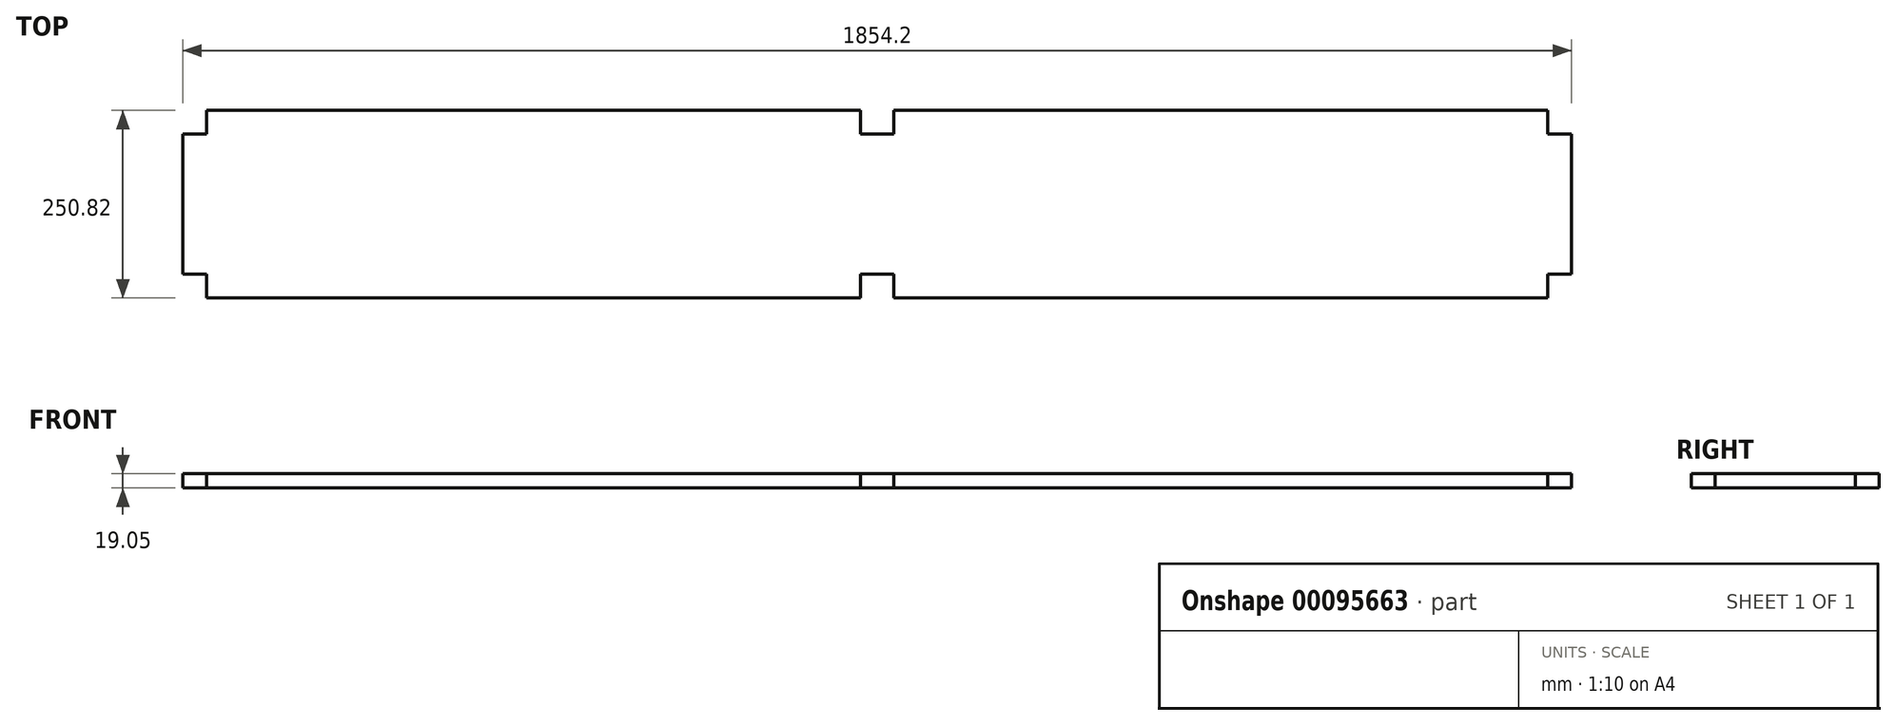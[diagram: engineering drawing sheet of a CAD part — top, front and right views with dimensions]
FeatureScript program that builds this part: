
annotation { "Feature Type Name" : "Feature", "Feature Type Description" : "" }
export const myFeature = defineFeature(function(context is Context, id is Id, definition is map)
    precondition{}
    {
        {
            var Q0;
            Q0=qCreatedBy(makeId("Top.planeOp"),FACE);
            var sketch = newSketch(context, id + "F0", { "sketchPlane" : qUnion([Q0])});
            skLineSegment(sketch, "E0.top", {"start": v(-895.35, 125.41) * mm, "end": v(-22.22, 125.41) * mm});
            skLineSegment(sketch, "E0.left", {"start": v(-927.1, -93.66) * mm, "end": v(-927.1, 93.66) * mm});
            skLineSegment(sketch, "E0.right", {"start": v(927.1, -93.66) * mm, "end": v(927.1, 93.66) * mm});
            skLineSegment(sketch, "E1", {"start": v(895.35, -125.41) * mm, "end": v(22.23, -125.41) * mm});
            skLineSegment(sketch, "E2.top", {"start": v(-927.1, 93.66) * mm, "end": v(-895.35, 93.66) * mm});
            skLineSegment(sketch, "E2.right", {"start": v(-895.35, 125.41) * mm, "end": v(-895.35, 93.66) * mm});
            skLineSegment(sketch, "E3.0.1.1", {"start": v(-927.1, -93.66) * mm, "end": v(-895.35, -93.66) * mm});
            skLineSegment(sketch, "E3.0.1.2", {"start": v(-895.35, -93.66) * mm, "end": v(-895.35, -125.41) * mm});
            skLineSegment(sketch, "E3.1.0.0", {"start": v(-22.22, 93.66) * mm, "end": v(22.23, 93.66) * mm});
            skLineSegment(sketch, "E3.1.0.2", {"start": v(22.23, 125.41) * mm, "end": v(22.23, 93.66) * mm});
            skLineSegment(sketch, "E3.1.0.3", {"start": v(-22.22, 125.41) * mm, "end": v(-22.22, 93.66) * mm});
            skLineSegment(sketch, "E3.1.1.1", {"start": v(-22.22, -93.66) * mm, "end": v(22.23, -93.66) * mm});
            skLineSegment(sketch, "E3.1.1.2", {"start": v(22.23, -93.66) * mm, "end": v(22.23, -125.41) * mm});
            skLineSegment(sketch, "E3.1.1.3", {"start": v(-22.22, -93.66) * mm, "end": v(-22.22, -125.41) * mm});
            skLineSegment(sketch, "E3.2.0.0", {"start": v(895.35, 93.66) * mm, "end": v(927.1, 93.66) * mm});
            skLineSegment(sketch, "E3.2.0.3", {"start": v(895.35, 125.41) * mm, "end": v(895.35, 93.66) * mm});
            skLineSegment(sketch, "E3.2.1.1", {"start": v(895.35, -93.66) * mm, "end": v(927.1, -93.66) * mm});
            skLineSegment(sketch, "E3.2.1.3", {"start": v(895.35, -93.66) * mm, "end": v(895.35, -125.41) * mm});
            skLineSegment(sketch, "E3.direction1", {"start": v(-927.1, 93.66) * mm, "end": v(-22.22, 93.66) * mm, "construction": true});
            skLineSegment(sketch, "E3.direction2", {"start": v(-939.8, 93.66) * mm, "end": v(-939.8, -138.11) * mm, "construction": true});
            skLineSegment(sketch, "E4.trimOffspring", {"start": v(22.23, 125.41) * mm, "end": v(895.35, 125.41) * mm});
            skPoint(sketch, "E5.orphan", {"position": v(-22.22, 138.11) * mm});
            skLineSegment(sketch, "E6.trimOffspring", {"start": v(-22.22, -125.41) * mm, "end": v(-895.35, -125.41) * mm});
            skPoint(sketch, "E7.orphan", {"position": v(-22.22, -138.11) * mm});
            skPoint(sketch, "E8.orphan", {"position": v(22.23, -138.11) * mm});
            skPoint(sketch, "E9.orphan", {"position": v(939.8, -93.66) * mm});
            skPoint(sketch, "E10.orphan", {"position": v(895.35, -138.11) * mm});
            skPoint(sketch, "E11.orphan", {"position": v(939.8, 93.66) * mm});
            skPoint(sketch, "E12.orphan", {"position": v(-895.35, 138.11) * mm});
            skSolve(sketch);
        }
        {
            var Q0;
            Q0=makeQuery(id+"F0.imprint","IMPRINT",FACE,{"disambiguationData":[TD([[makeQuery(id+"F0.imprint","IMPRINT",EDGE,{"derivedFrom":sQuery(id+"F0.wireOp",EDGE,"E0.top")}),-1.0]])]});
            extrude(context, id + "F1", {"entities" : qUnion([Q0]), "depth" : 19.05 * mm});
        }
    });
